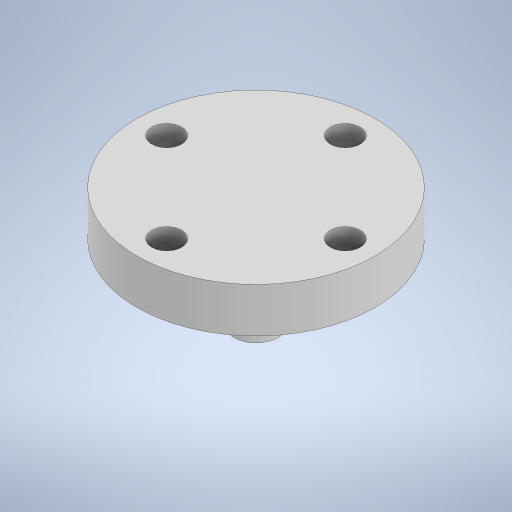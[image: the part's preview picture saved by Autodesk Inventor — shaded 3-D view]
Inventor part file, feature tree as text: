
AUTODESK INVENTOR PART (.ipt)
format: ipt  version: 2024.2 (Build 282272000, 272)  size: 218,624 bytes
history: native  units: mm
features: extrude x2, other x1, sketch x1
ambient origin geometry x8: Origin, YZ Plane, XZ Plane, XY Plane, X Axis, Y Axis, Z Axis, Center Point
bodies: Body1 (feature_tree)
feature tree (4):
  other  "Твердое тело1"
  sketch  "Эскиз1"
  extrude  "Выдавливание1"  Depth=16.0mm
  extrude  "Выдавливание2"  Depth=2.0mm
